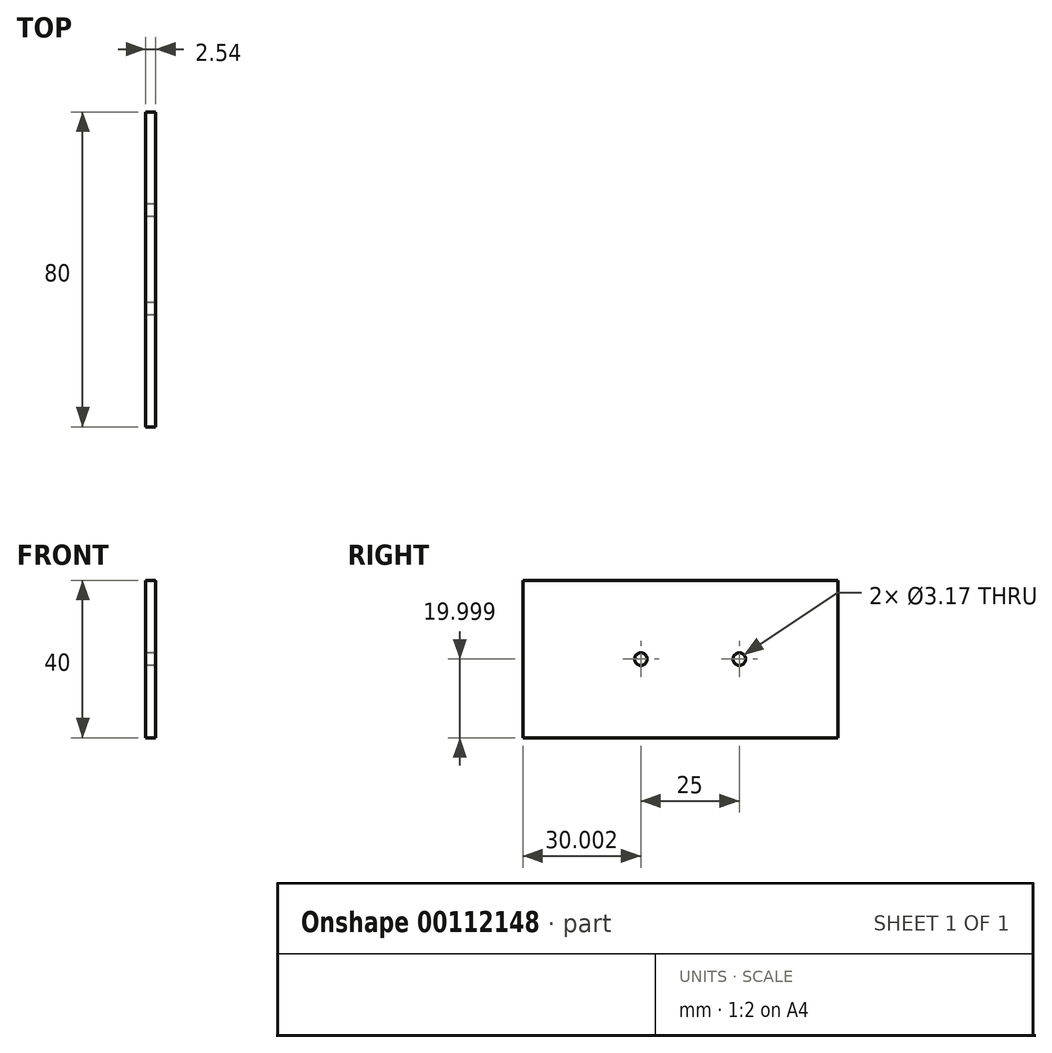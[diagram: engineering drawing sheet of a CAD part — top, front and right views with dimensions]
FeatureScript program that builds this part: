
annotation { "Feature Type Name" : "Feature", "Feature Type Description" : "" }
export const myFeature = defineFeature(function(context is Context, id is Id, definition is map)
    precondition{}
    {
        {
            var Q0;
            Q0=qCreatedBy(makeId("Right.planeOp"),FACE);
            var sketch = newSketch(context, id + "F0", { "sketchPlane" : qUnion([Q0])});
            skLineSegment(sketch, "E0.bottom", {"start": v(-37.37, -12.22) * mm, "end": v(42.63, -12.22) * mm});
            skLineSegment(sketch, "E0.top", {"start": v(-37.37, 27.78) * mm, "end": v(42.63, 27.78) * mm});
            skLineSegment(sketch, "E0.left", {"start": v(-37.37, -12.22) * mm, "end": v(-37.37, 27.78) * mm});
            skLineSegment(sketch, "E0.right", {"start": v(42.63, -12.22) * mm, "end": v(42.63, 27.78) * mm});
            skPoint(sketch, "E1.start.orphan", {"position": v(-37.37, 7.78) * mm});
            skCircle(sketch, "E2", {"center": v(-7.37, 7.78) * mm, "radius": 1.59 * mm});
            skCircle(sketch, "E3", {"center": v(17.63, 7.78) * mm, "radius": 1.59 * mm});
            skSolve(sketch);
        }
        {
            var Q0;
            Q0=makeQuery(id+"F0.imprint","IMPRINT",FACE,{"disambiguationData":[TD([[makeQuery(id+"F0.imprint","IMPRINT",EDGE,{"derivedFrom":sQuery(id+"F0.wireOp",EDGE,"E0.bottom")}),1.0]])]});
            extrude(context, id + "F1", {"entities" : qUnion([Q0]), "depth" : 2.54 * mm});
        }
    });
